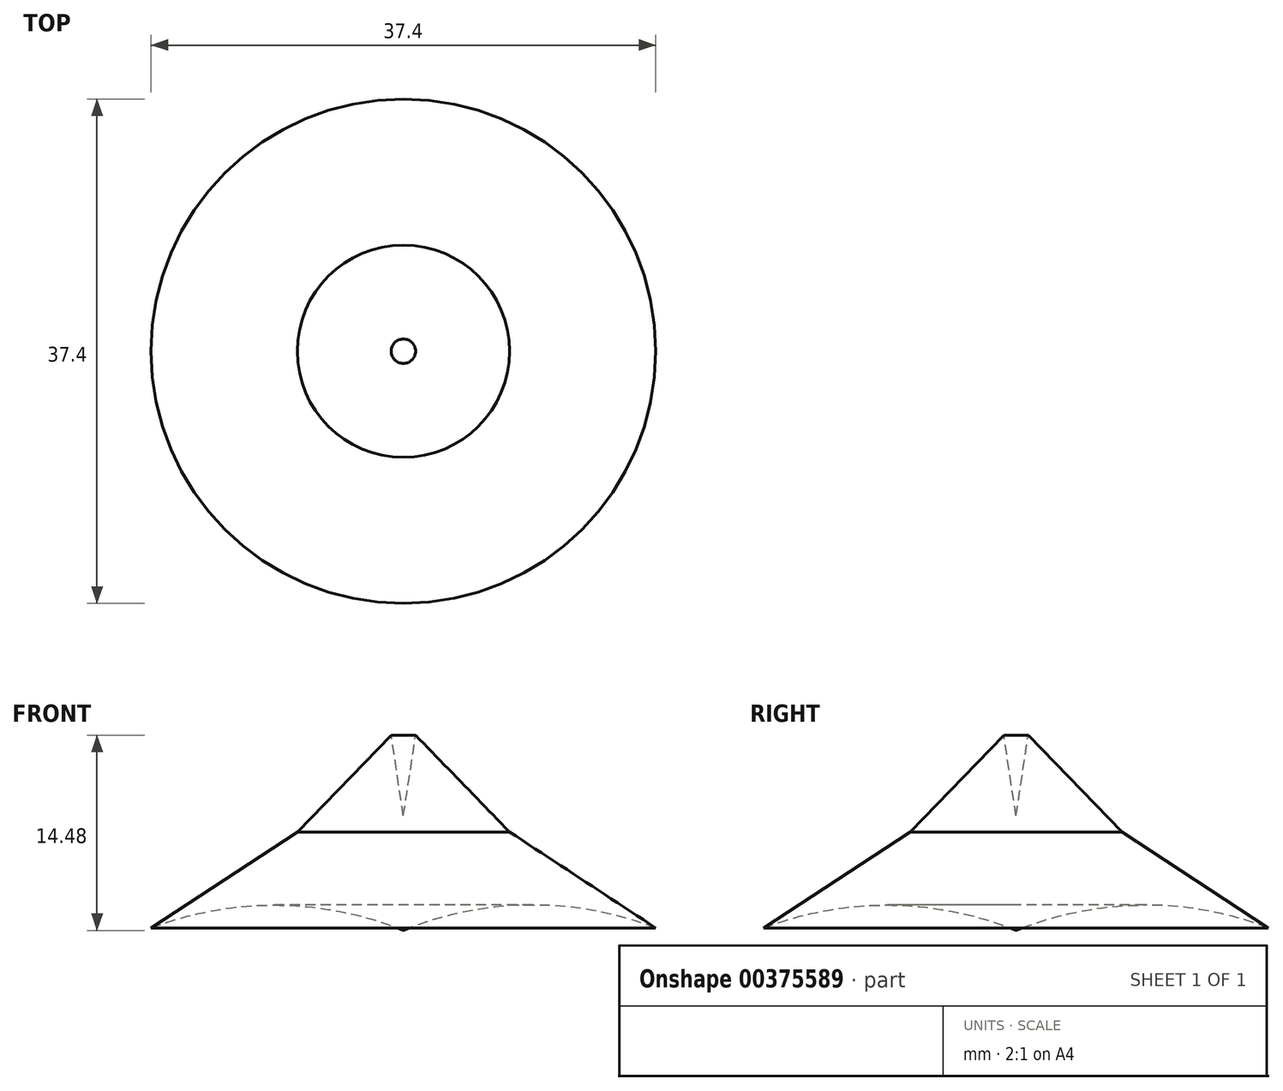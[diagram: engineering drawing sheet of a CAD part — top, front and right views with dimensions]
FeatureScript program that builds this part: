
annotation { "Feature Type Name" : "Feature", "Feature Type Description" : "" }
export const myFeature = defineFeature(function(context is Context, id is Id, definition is map)
    precondition{}
    {
        {
            var Q0;
            Q0=qCreatedBy(makeId("Front.planeOp"),FACE);
            var sketch = newSketch(context, id + "F0", { "sketchPlane" : qUnion([Q0])});
            skArc(sketch, "E0", {"start": v(-18.7, 12.11) * mm, "mid": v(-33.2, -20.94) * mm, "end": v(0, -35.12) * mm});
            skLineSegment(sketch, "E1", {"start": v(0, 11.93) * mm, "end": v(0, -35.12) * mm});
            skLineSegment(sketch, "E2", {"start": v(-18.7, 12.11) * mm, "end": v(-7.86, 19.23) * mm});
            skLineSegment(sketch, "E3", {"start": v(-7.86, 19.23) * mm, "end": v(-3.93, 19.82) * mm});
            skLineSegment(sketch, "E4", {"start": v(0, 20.42) * mm, "end": v(0, 11.93) * mm});
            skLineSegment(sketch, "E5", {"start": v(0, 20.42) * mm, "end": v(-0.9, 26.4) * mm});
            skLineSegment(sketch, "E6", {"start": v(-3.93, 20.42) * mm, "end": v(-0.9, 26.4) * mm});
            skPoint(sketch, "E6.startSnap0", {"position": v(-3.93, 19.82) * mm});
            skPoint(sketch, "E7.orphan", {"position": v(-7.86, 13.75) * mm});
            skLineSegment(sketch, "E8", {"start": v(0, -35.12) * mm, "end": v(0, 20.42) * mm});
            skLineSegment(sketch, "E9", {"start": v(-7.86, 19.23) * mm, "end": v(-0.9, 26.4) * mm});
            skSolve(sketch);
        }
        {
            var Q0;
            Q0 = qSketchRegion(id + "F0", true);
            var Q1;
            Q1=sQuery(id+"F0.wireOp",EDGE,"E1");
            revolve(context, id + "F1", {"entities" : qUnion([Q0]), "axis" : qUnion([Q1]), "revolveType" : RevolveType.FULL});
        }
        {
            var Q0;
            Q0=qCreatedBy(makeId("Front.planeOp"),FACE);
            var sketch = newSketch(context, id + "F2", { "sketchPlane" : qUnion([Q0])});
            skEllipse(sketch, "E10", {"center": v(0, -12.56) * mm, "majorRadius": 29.4 * mm, "minorRadius": 18.28 * mm, "majorAxis": v(1, 0)});
            skLineSegment(sketch, "E11", {"start": v(0, 5.72) * mm, "end": v(0, -30.84) * mm});
            skSolve(sketch);
        }
        {
            var Q0;
            Q0 = qSketchRegion(id + "F2", true);
            extrude(context, id + "F3", {"entities" : qUnion([Q0]), "operationType" : NewBodyOperationType.REMOVE, "oppositeDirection" : true, "depth" : 66.8 * mm});
        }
    });
